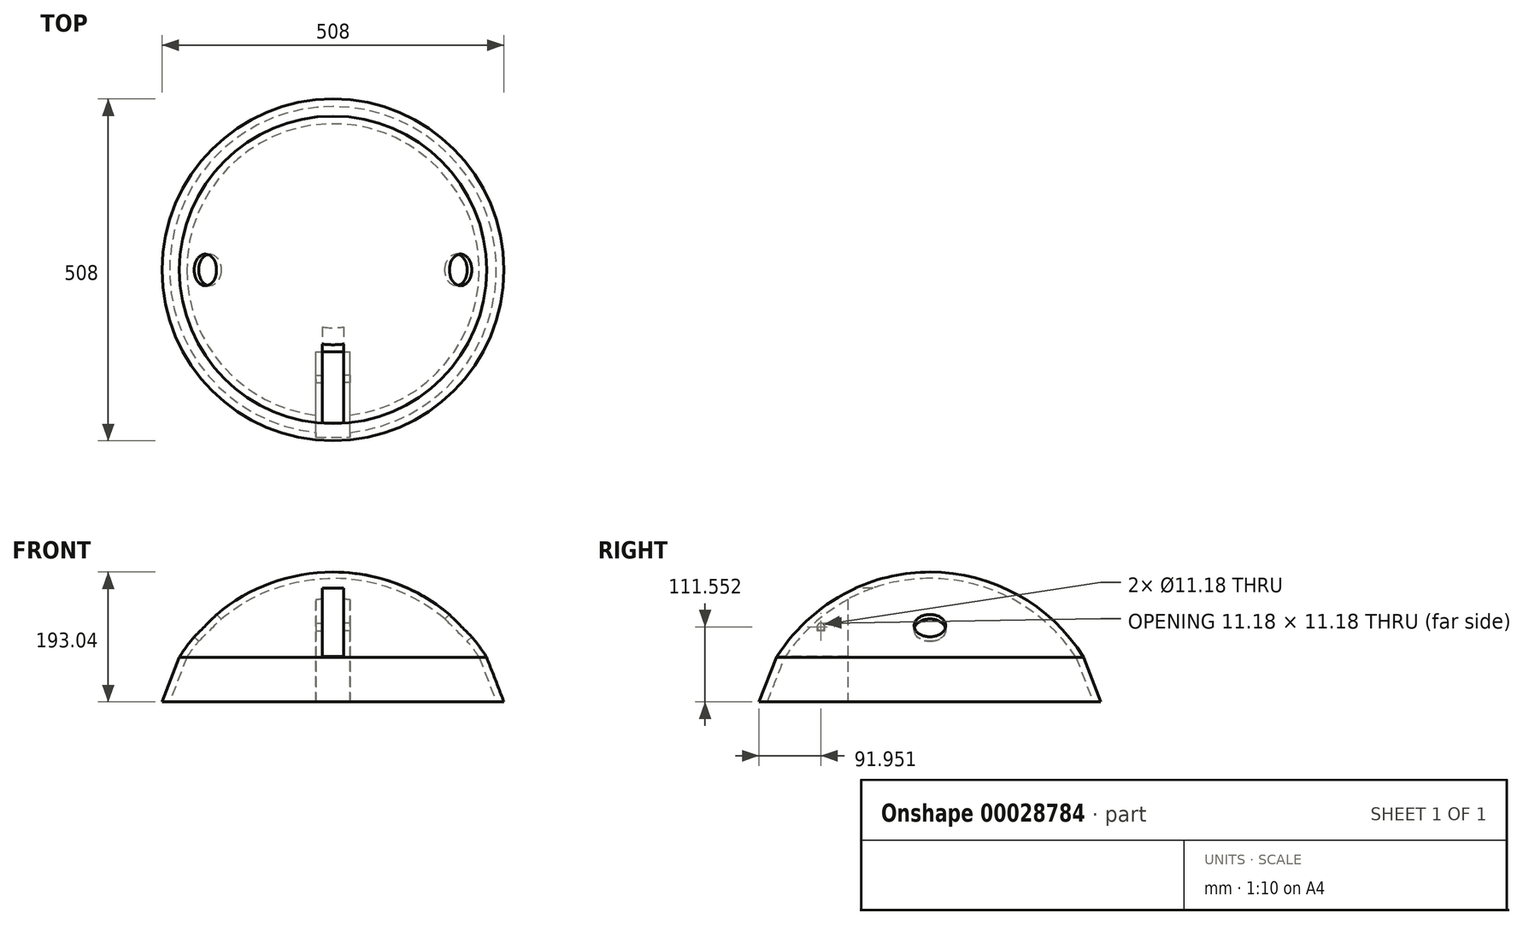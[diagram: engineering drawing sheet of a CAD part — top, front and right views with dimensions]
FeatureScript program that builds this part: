
annotation { "Feature Type Name" : "Feature", "Feature Type Description" : "" }
export const myFeature = defineFeature(function(context is Context, id is Id, definition is map)
    precondition{}
    {
        {
            var Q0;
            Q0=qCreatedBy(makeId("Front.planeOp"),FACE);
            var sketch = newSketch(context, id + "F0", { "sketchPlane" : qUnion([Q0])});
            skArc(sketch, "E0", {"start": v(228.6, 142.24) * mm, "mid": v(228.51, 142.38) * mm, "end": v(228.42, 142.53) * mm});
            skLineSegment(sketch, "E1", {"start": v(0, 269.24) * mm, "end": v(0, -269.24) * mm, "construction": true});
            skLineSegment(sketch, "E2", {"start": v(228.6, 142.53) * mm, "end": v(228.42, 142.53) * mm, "construction": true});
            skLineSegment(sketch, "E3", {"start": v(-279, 76.33) * mm, "end": v(507.36, 76.33) * mm, "construction": true});
            skLineSegment(sketch, "E4", {"start": v(-228.42, 142.53) * mm, "end": v(-228.42, 76.33) * mm, "construction": true});
            skLineSegment(sketch, "E5", {"start": v(-254, 174.53) * mm, "end": v(-254, 8.55) * mm, "construction": true});
            skLineSegment(sketch, "E6", {"start": v(-228.42, 142.53) * mm, "end": v(-254, 76.33) * mm});
            skLineSegment(sketch, "E7", {"start": v(-217.27, 142.53) * mm, "end": v(217.27, 142.53) * mm, "construction": true});
            skArc(sketch, "E8.trimOffspring", {"start": v(254, 54.82) * mm, "mid": v(251.42, 65.63) * mm, "end": v(248.38, 76.33) * mm});
            skArc(sketch, "E9.trimOffspring", {"start": v(0, 259.85) * mm, "mid": v(-123.46, 228.64) * mm, "end": v(-217.27, 142.53) * mm});
            skLineSegment(sketch, "E10", {"start": v(-217.27, 142.53) * mm, "end": v(-242.85, 76.33) * mm});
            skLineSegment(sketch, "E11", {"start": v(-254, 76.33) * mm, "end": v(-242.85, 76.33) * mm});
            skLineSegment(sketch, "E12", {"start": v(0, 269.24) * mm, "end": v(0, 259.85) * mm});
            skPoint(sketch, "E13.end.orphan", {"position": v(243.42, 76.33) * mm});
            skPoint(sketch, "E14.orphan", {"position": v(232.09, 76.33) * mm});
            skArc(sketch, "E15.trimOffspring", {"start": v(0, 269.24) * mm, "mid": v(-130.6, 235.44) * mm, "end": v(-228.42, 142.53) * mm});
            skLineSegment(sketch, "E16.trimOffspring", {"start": v(0, 142.53) * mm, "end": v(-228.42, 142.53) * mm, "construction": true});
            skLineSegment(sketch, "E17", {"start": v(0, 259.85) * mm, "end": v(-183.52, 76.33) * mm, "construction": true});
            skSolve(sketch);
        }
        {
            var Q0;
            Q0=makeQuery(id+"F0.imprint","IMPRINT",FACE,{"disambiguationData":[TD([[makeQuery(id+"F0.imprint","IMPRINT",EDGE,{"derivedFrom":sQuery(id+"F0.wireOp",EDGE,"E6")}),1.0]])]});
            var Q1;
            Q1=sQuery(id+"F0.wireOp",EDGE,"E1");
            revolve(context, id + "F1", {"entities" : qUnion([Q0]), "axis" : qUnion([Q1]), "revolveType" : RevolveType.FULL});
        }
        {
            var Q0;
            Q0=qCreatedBy(makeId("Front.planeOp"),FACE);
            cPlane(context, id + "F2", {"entities" : qUnion([Q0]), "cplaneType" : CPlaneType.OFFSET, "offset" : 279.4 * mm, "width" : 152.4 * mm, "height" : 152.4 * mm});
        }
        {
            var Q0;
            Q0=qCreatedBy(id+"F2.planeOp",FACE);
            var sketch = newSketch(context, id + "F3", { "sketchPlane" : qUnion([Q0])});
            skLineSegment(sketch, "E18", {"start": v(0, 0) * mm, "end": v(0, 312.19) * mm, "construction": true});
            skLineSegment(sketch, "E19", {"start": v(16, 234.4) * mm, "end": v(16, 133.44) * mm, "construction": true});
            skLineSegment(sketch, "E20", {"start": v(-16, 133.44) * mm, "end": v(-16, 233.85) * mm, "construction": true});
            skLineSegment(sketch, "E21.bottom", {"start": v(-16, 143.58) * mm, "end": v(16, 143.58) * mm});
            skLineSegment(sketch, "E21.top", {"start": v(-16, 245.18) * mm, "end": v(16, 245.18) * mm});
            skLineSegment(sketch, "E21.left", {"start": v(-16, 143.58) * mm, "end": v(-16, 245.18) * mm});
            skLineSegment(sketch, "E21.right", {"start": v(16, 143.58) * mm, "end": v(16, 245.18) * mm});
            skSolve(sketch);
        }
        {
            var Q0;
            Q0=qCreatedBy(makeId("Front.planeOp"),FACE);
            var sketch = newSketch(context, id + "F4", { "sketchPlane" : qUnion([Q0])});
            skLineSegment(sketch, "E22", {"start": v(0, 0) * mm, "end": v(244.42, 244.42) * mm, "construction": true});
            skLineSegment(sketch, "E23", {"start": v(0, 0) * mm, "end": v(-244.42, 244.42) * mm, "construction": true});
            skLineSegment(sketch, "E24", {"start": v(190.46, 190.46) * mm, "end": v(190.46, -35.98) * mm, "construction": true});
            skLineSegment(sketch, "E25", {"start": v(-190.88, 190.88) * mm, "end": v(-190.88, -57.56) * mm, "construction": true});
            skSolve(sketch);
        }
        {
            var Q0;
            Q0=sQuery(id+"F4.wireOp",EDGE,"E22");
            var Q1;
            Q1=qCreatedBy(makeId("Front.planeOp"),FACE);
            cPlane(context, id + "F5", {"entities" : qUnion([Q0, Q1]), "cplaneType" : CPlaneType.LINE_ANGLE, "offset" : 152.4 * mm, "angle" : 90 * degree, "width" : 152.4 * mm, "height" : 152.4 * mm});
        }
        {
            var Q0;
            Q0=qCreatedBy(id+"F5.planeOp",FACE);
            var sketch = newSketch(context, id + "F6", { "sketchPlane" : qUnion([Q0])});
            skCircle(sketch, "E26", {"center": v(0, 0) * mm, "radius": 23.5 * mm});
            skSolve(sketch);
        }
        {
            var Q0;
            Q0=makeQuery(id+"F6.imprint","IMPRINT",FACE,{"disambiguationData":[TD([[makeQuery(id+"F6.imprint","IMPRINT",EDGE,{"derivedFrom":sQuery(id+"F6.wireOp",EDGE,"E26")}),1.0]])]});
            extrude(context, id + "F7", {"entities" : qUnion([Q0]), "operationType" : NewBodyOperationType.REMOVE, "depth" : 304.8 * mm});
        }
        {
            var Q0;
            Q0=sQuery(id+"F4.wireOp",EDGE,"E23");
            cPlane(context, id + "F8", {"entities" : qUnion([Q0]), "cplaneType" : CPlaneType.LINE_ANGLE, "offset" : 152.4 * mm, "angle" : 90 * degree, "width" : 152.4 * mm, "height" : 152.4 * mm});
        }
        {
            var Q0;
            Q0=qCreatedBy(id+"F8.planeOp",FACE);
            var sketch = newSketch(context, id + "F9", { "sketchPlane" : qUnion([Q0])});
            skCircle(sketch, "E27", {"center": v(0, 0) * mm, "radius": 23.5 * mm});
            skSolve(sketch);
        }
        {
            var Q0;
            Q0=makeQuery(id+"F9.imprint","IMPRINT",FACE,{"disambiguationData":[TD([[makeQuery(id+"F9.imprint","IMPRINT",EDGE,{"derivedFrom":sQuery(id+"F9.wireOp",EDGE,"E27")}),1.0]])]});
            var Q1;
            Q1=sQuery(id+"F9.wireOp",EDGE,"E27");
            extrude(context, id + "F10", {"entities" : qUnion([Q0]), "operationType" : NewBodyOperationType.REMOVE, "surfaceEntities" : qUnion([Q1]), "depth" : 304.8 * mm});
        }
        {
            var Q0;
            Q0=qCreatedBy(makeId("Top.planeOp"),FACE);
            cPlane(context, id + "F11", {"entities" : qUnion([Q0]), "cplaneType" : CPlaneType.OFFSET, "offset" : 76.2 * mm, "width" : 152.4 * mm, "height" : 152.4 * mm});
        }
        {
            var Q0;
            Q0=qCreatedBy(id+"F11.planeOp",FACE);
            var sketch = newSketch(context, id + "F12", { "sketchPlane" : qUnion([Q0])});
            skLineSegment(sketch, "E28", {"start": v(0, 0) * mm, "end": v(0, -248.92) * mm, "construction": true});
            skLineSegment(sketch, "E29.bottom", {"start": v(0, -248.92) * mm, "end": v(-25.4, -248.92) * mm});
            skLineSegment(sketch, "E29.top", {"start": v(0, -121.92) * mm, "end": v(-25.4, -121.92) * mm});
            skLineSegment(sketch, "E29.right", {"start": v(-25.4, -248.92) * mm, "end": v(-25.4, -121.92) * mm});
            skLineSegment(sketch, "E30.bottom", {"start": v(0, -248.92) * mm, "end": v(25.4, -248.92) * mm});
            skLineSegment(sketch, "E30.top", {"start": v(0, -121.92) * mm, "end": v(25.4, -121.92) * mm});
            skLineSegment(sketch, "E30.right", {"start": v(25.4, -248.92) * mm, "end": v(25.4, -121.92) * mm});
            skSolve(sketch);
        }
        {
            var Q0;
            Q0=makeQuery(id+"F12.imprint","IMPRINT",FACE,{"disambiguationData":[TD([[makeQuery(id+"F12.imprint","IMPRINT",EDGE,{"derivedFrom":sQuery(id+"F12.wireOp",EDGE,"E29.bottom")}),-1.0]])]});
            extrude(context, id + "F13", {"entities" : qUnion([Q0]), "operationType" : NewBodyOperationType.ADD, "endBound" : BoundingType.UP_TO_NEXT, "depth" : 25.4 * mm});
        }
        {
            var Q0;
            Q0=makeQuery(id+"F3.imprint","IMPRINT",FACE,{"disambiguationData":[TD([[makeQuery(id+"F3.imprint","IMPRINT",EDGE,{"derivedFrom":sQuery(id+"F3.wireOp",EDGE,"E21.bottom")}),1.0]])]});
            extrude(context, id + "F14", {"entities" : qUnion([Q0]), "operationType" : NewBodyOperationType.REMOVE, "oppositeDirection" : true, "depth" : 228.6 * mm});
        }
        {
            var Q0;
            Q0=qCreatedBy(makeId("Right.planeOp"),FACE);
            var sketch = newSketch(context, id + "F15", { "sketchPlane" : qUnion([Q0])});
            skLineSegment(sketch, "E31.bottom", {"start": v(-116.31, 234.35) * mm, "end": v(-220.22, 234.35) * mm});
            skLineSegment(sketch, "E31.top", {"start": v(-116.31, 145) * mm, "end": v(-220.22, 145) * mm});
            skLineSegment(sketch, "E31.left", {"start": v(-116.31, 234.35) * mm, "end": v(-116.31, 145) * mm});
            skLineSegment(sketch, "E31.right", {"start": v(-220.22, 234.35) * mm, "end": v(-220.22, 145) * mm});
            skCircle(sketch, "E32", {"center": v(-162.05, 187.75) * mm, "radius": 53.34 * mm});
            skCircle(sketch, "E33", {"center": v(-162.05, 187.75) * mm, "radius": 5.59 * mm});
            skSolve(sketch);
        }
        {
            var Q0;
            Q0=makeQuery(id+"F15.imprint","IMPRINT",FACE,{"disambiguationData":[TD([[makeQuery(id+"F15.imprint","IMPRINT",EDGE,{"derivedFrom":sQuery(id+"F15.wireOp",EDGE,"E33")}),1.0]])]});
            extrude(context, id + "F16", {"entities" : qUnion([Q0]), "operationType" : NewBodyOperationType.REMOVE, "oppositeDirection" : true, "depth" : 50.8 * mm});
        }
        {
            var Q0;
            Q0=makeQuery(id+"F15.imprint","IMPRINT",FACE,{"disambiguationData":[TD([[makeQuery(id+"F15.imprint","IMPRINT",EDGE,{"derivedFrom":sQuery(id+"F15.wireOp",EDGE,"E33")}),1.0]])]});
            extrude(context, id + "F17", {"entities" : qUnion([Q0]), "operationType" : NewBodyOperationType.REMOVE, "depth" : 50.8 * mm});
        }
    });
